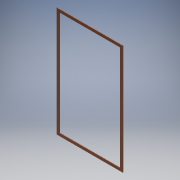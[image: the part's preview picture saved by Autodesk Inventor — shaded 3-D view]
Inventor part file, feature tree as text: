
AUTODESK INVENTOR PART (.ipt)
format: ipt  version: 2017 (Build 210142000, 142)  size: 101,888 bytes
history: native  units: mm
features: extrude x1, sketch x1
ambient origin geometry x8: Origin, YZ Plane, XZ Plane, XY Plane, X Axis, Y Axis, Z Axis, Center Point
bodies: Volumenkörper1 (feature_tree)
feature tree (2):
  extrude  "Extrusion1"  Depth=1200.0mm
  sketch  "Skizze1"  dims[d2=2000.0mm d3=1200.0mm d4=50.0mm d5=10.0mm d6=0.0mm]
